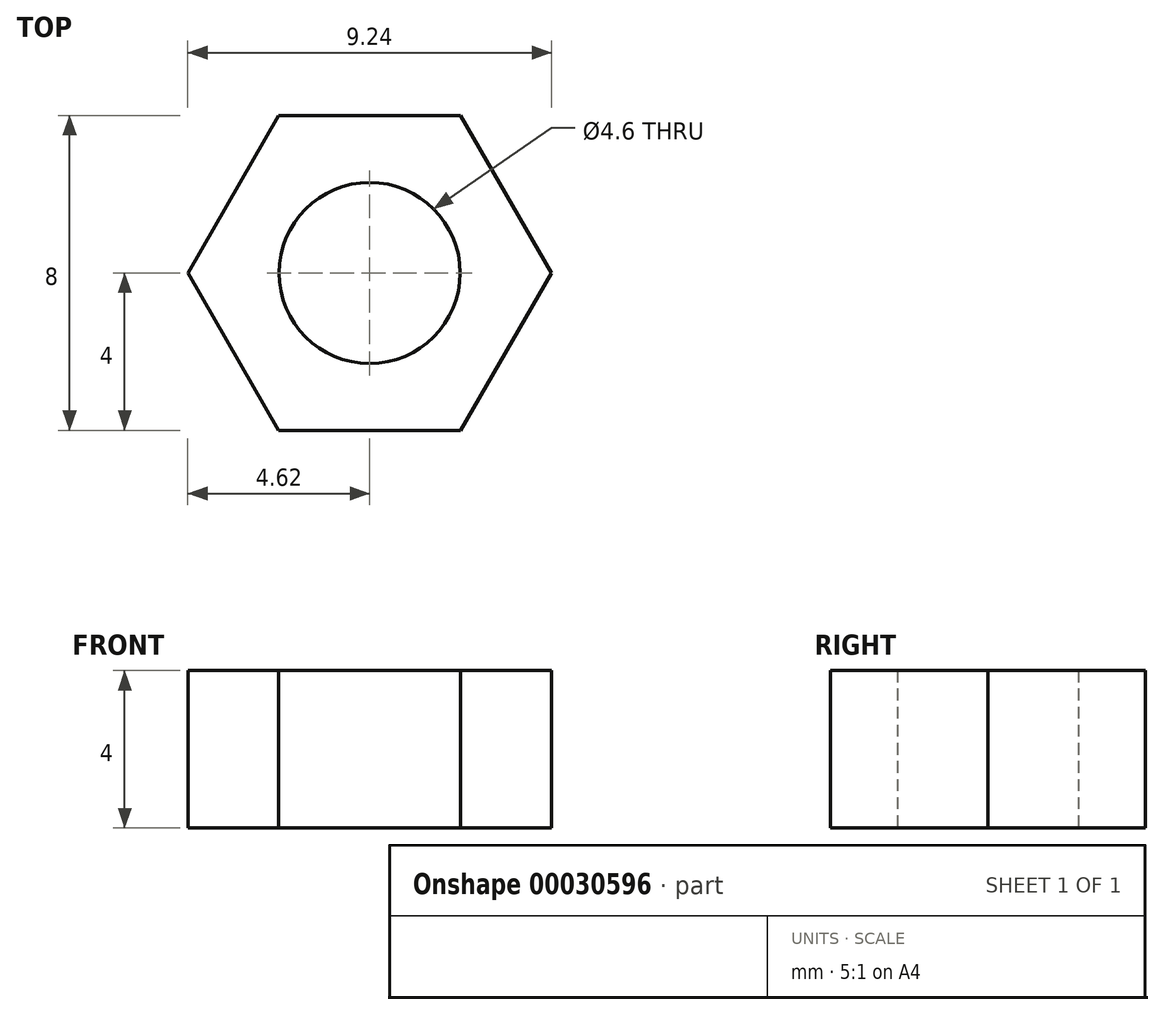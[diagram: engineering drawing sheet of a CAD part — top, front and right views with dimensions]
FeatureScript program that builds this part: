
annotation { "Feature Type Name" : "Feature", "Feature Type Description" : "" }
export const myFeature = defineFeature(function(context is Context, id is Id, definition is map)
    precondition{}
    {
        {
            assignVariable(context, id + "F0", {"name" : "NutT", "anyValue" : 4});
        }
        {
            var Q0;
            Q0=qCreatedBy(makeId("Top.planeOp"),FACE);
            var sketch = newSketch(context, id + "F1", { "sketchPlane" : qUnion([Q0])});
            skCircle(sketch, "E0.cCircle", {"center": v(0, 0) * mm, "radius": 4 * mm, "construction": true});
            skLineSegment(sketch, "E0.0", {"start": v(-4.62, 0) * mm, "end": v(-2.3, 4) * mm});
            skLineSegment(sketch, "E0.1", {"start": v(-2.3, 4) * mm, "end": v(2.3, 4) * mm});
            skLineSegment(sketch, "E0.2", {"start": v(2.3, 4) * mm, "end": v(4.62, 0) * mm});
            skLineSegment(sketch, "E0.3", {"start": v(4.62, 0) * mm, "end": v(2.3, -4) * mm});
            skLineSegment(sketch, "E0.4", {"start": v(2.3, -4) * mm, "end": v(-2.3, -4) * mm});
            skLineSegment(sketch, "E0.5", {"start": v(-2.3, -4) * mm, "end": v(-4.62, 0) * mm});
            skPoint(sketch, "E0.0.midPoint", {"position": v(-3.46, 2) * mm});
            skCircle(sketch, "E1", {"center": v(0, 0) * mm, "radius": 2.3 * mm});
            skSolve(sketch);
        }
        {
            var Q0;
            Q0 = qSketchRegion(id + "F1", true);
            extrude(context, id + "F2", {"entities" : qUnion([Q0]), "depth" : (getVariable(context, 'NutT')) * mm});
        }
    });
